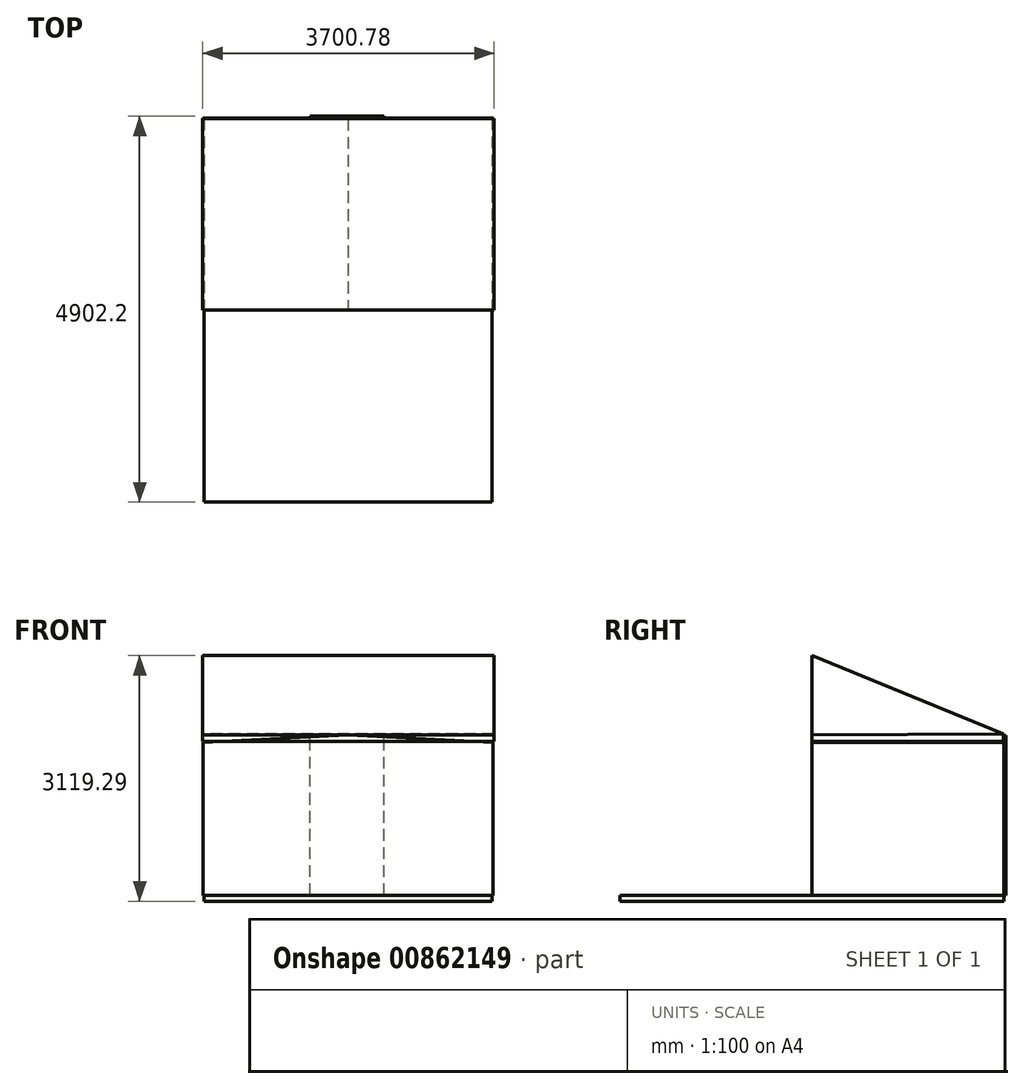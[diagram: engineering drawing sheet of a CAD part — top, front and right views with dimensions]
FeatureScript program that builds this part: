
annotation { "Feature Type Name" : "Feature", "Feature Type Description" : "" }
export const myFeature = defineFeature(function(context is Context, id is Id, definition is map)
    precondition{}
    {
        {
            var Q0;
            Q0=qCreatedBy(makeId("Top.planeOp"),FACE);
            var sketch = newSketch(context, id + "F0", { "sketchPlane" : qUnion([Q0])});
            skLineSegment(sketch, "E0.bottom", {"start": v(1828.8, 2438.4) * mm, "end": v(-1828.8, 2438.4) * mm});
            skLineSegment(sketch, "E0.top", {"start": v(1828.8, -2438.4) * mm, "end": v(-1828.8, -2438.4) * mm});
            skLineSegment(sketch, "E0.left", {"start": v(1828.8, 2438.4) * mm, "end": v(1828.8, -2438.4) * mm});
            skLineSegment(sketch, "E0.right", {"start": v(-1828.8, 2438.4) * mm, "end": v(-1828.8, -2438.4) * mm});
            skPoint(sketch, "E0.middle", {"position": v(0, 0) * mm});
            skPoint(sketch, "E1", {"position": v(1828.8, -2438.4) * mm});
            skPoint(sketch, "E2", {"position": v(-1828.8, -2438.4) * mm});
            skPoint(sketch, "E3", {"position": v(-1828.8, 2438.4) * mm});
            skPoint(sketch, "E4", {"position": v(1828.8, 2438.4) * mm});
            skSolve(sketch);
        }
        {
            var Q0;
            Q0=qCreatedBy(makeId("Front.planeOp"),FACE);
            var sketch = newSketch(context, id + "F1", { "sketchPlane" : qUnion([Q0])});
            skLineSegment(sketch, "E5", {"start": v(1843.43, 0) * mm, "end": v(1843.43, 1941.23) * mm});
            skLineSegment(sketch, "E6", {"start": v(1843.43, 1941.23) * mm, "end": v(0, 2036.83) * mm});
            skLineSegment(sketch, "E7", {"start": v(0, 2036.83) * mm, "end": v(-1839.49, 1941.23) * mm});
            skLineSegment(sketch, "E8", {"start": v(-1839.49, 1941.23) * mm, "end": v(-1839.49, 0) * mm});
            skLineSegment(sketch, "E9", {"start": v(1843.43, 0) * mm, "end": v(-1839.49, 0) * mm});
            skSolve(sketch);
        }
        {
            var Q0;
            Q0=makeQuery(id+"F1.imprint","IMPRINT",FACE,{"disambiguationData":[TD([[makeQuery(id+"F1.imprint","IMPRINT",EDGE,{"derivedFrom":sQuery(id+"F1.wireOp",EDGE,"E5")}),1.0]])]});
            extrude(context, id + "F2", {"entities" : qUnion([Q0]), "oppositeDirection" : true, "depth" : 2438.4 * mm, "offsetDistance" : 25.4 * mm});
        }
        {
            var Q0;
            Q0=qCreatedBy(makeId("Right.planeOp"),FACE);
            var sketch = newSketch(context, id + "F3", { "sketchPlane" : qUnion([Q0])});
            skLineSegment(sketch, "E10", {"start": v(2432.25, 2051.92) * mm, "end": v(0, 3043.09) * mm});
            skLineSegment(sketch, "E11", {"start": v(0, 3043.09) * mm, "end": v(0, 2036.83) * mm});
            skLineSegment(sketch, "E12", {"start": v(0, 2036.83) * mm, "end": v(2432.25, 2051.92) * mm});
            skSolve(sketch);
        }
        {
            var Q0;
            Q0=makeQuery(id+"F3.imprint","IMPRINT",FACE,{"disambiguationData":[TD([[makeQuery(id+"F3.imprint","IMPRINT",EDGE,{"derivedFrom":sQuery(id+"F3.wireOp",EDGE,"E10")}),1.0]])]});
            extrude(context, id + "F4", {"entities" : qUnion([Q0]), "depth" : 1856.74 * mm, "offsetDistance" : 25.4 * mm});
        }
        {
            var Q0;
            Q0=makeQuery(id+"F4.opExtrude","CAP_FACE",FACE,{"disambiguationData":[OSD([sQuery(id+"F3.wireOp",EDGE,"E10"),sQuery(id+"F3.wireOp",EDGE,"E11"),sQuery(id+"F3.wireOp",EDGE,"E12")])],"isStart":true});
            extrude(context, id + "F5", {"entities" : qUnion([Q0]), "operationType" : NewBodyOperationType.ADD, "depth" : 1844.04 * mm, "offsetDistance" : 25.4 * mm});
        }
        {
            var Q0;
            Q0=makeQuery(id+"F5.opExtrude","CAP_FACE",FACE,{"disambiguationData":[OSD([sQuery(id+"F3.wireOp",EDGE,"E10"),sQuery(id+"F3.wireOp",EDGE,"E11"),sQuery(id+"F3.wireOp",EDGE,"E12")])],"isStart":false});
            var sketch = newSketch(context, id + "F6", { "sketchPlane" : qUnion([Q0])});
            skLineSegment(sketch, "E13", {"start": v(-2432.25, 2051.92) * mm, "end": v(-2432.25, 1956.17) * mm});
            skLineSegment(sketch, "E14", {"start": v(-2432.25, 1956.17) * mm, "end": v(0, 1956.17) * mm});
            skLineSegment(sketch, "E15", {"start": v(0, 1956.17) * mm, "end": v(0, 2036.83) * mm});
            skLineSegment(sketch, "E16", {"start": v(0, 2036.83) * mm, "end": v(-2432.25, 2051.92) * mm});
            skSolve(sketch);
        }
        {
            var Q0;
            Q0=makeQuery(id+"F2.opExtrude","CAP_FACE",FACE,{"disambiguationData":[OSD([sQuery(id+"F1.wireOp",EDGE,"E5"),sQuery(id+"F1.wireOp",EDGE,"E6"),sQuery(id+"F1.wireOp",EDGE,"E7"),sQuery(id+"F1.wireOp",EDGE,"E8"),sQuery(id+"F1.wireOp",EDGE,"E9")])],"isStart":false});
            var sketch = newSketch(context, id + "F7", { "sketchPlane" : qUnion([Q0])});
            skLineSegment(sketch, "E17", {"start": v(-1843.43, 1941.23) * mm, "end": v(1839.49, 1941.23) * mm});
            skLineSegment(sketch, "E18", {"start": v(1839.49, 1941.23) * mm, "end": v(1839.49, 2036.83) * mm});
            skLineSegment(sketch, "E19", {"start": v(1839.49, 2036.83) * mm, "end": v(-1843.43, 2036.83) * mm});
            skLineSegment(sketch, "E20", {"start": v(-1843.43, 2036.83) * mm, "end": v(-1843.43, 1941.23) * mm});
            skSolve(sketch);
        }
        {
            var Q0;
            Q0=makeQuery(id+"F6.imprint","IMPRINT",FACE,{"disambiguationData":[TD([[makeQuery(id+"F6.imprint","IMPRINT",EDGE,{"derivedFrom":sQuery(id+"F6.wireOp",EDGE,"E13")}),1.0]])]});
            extrude(context, id + "F8", {"entities" : qUnion([Q0]), "oppositeDirection" : true, "depth" : 3700.78 * mm, "offsetDistance" : 25.4 * mm});
        }
        {
            var Q0;
            Q0=makeQuery(id+"F7.imprint","IMPRINT",FACE,{"disambiguationData":[TD([[makeQuery(id+"F7.imprint","IMPRINT",EDGE,{"derivedFrom":sQuery(id+"F7.wireOp",EDGE,"E17")}),-1.0]])]});
            var sketch = newSketch(context, id + "F9", { "sketchPlane" : qUnion([Q0])});
            skLineSegment(sketch, "E21", {"start": v(0, 0) * mm, "end": v(-457.2, 0) * mm});
            skLineSegment(sketch, "E22.bottom", {"start": v(-457.2, 0) * mm, "end": v(479.3, 0) * mm});
            skLineSegment(sketch, "E22.top", {"start": v(-457.2, 2032) * mm, "end": v(479.3, 2032) * mm});
            skLineSegment(sketch, "E22.left", {"start": v(-457.2, 0) * mm, "end": v(-457.2, 2032) * mm});
            skLineSegment(sketch, "E22.right", {"start": v(479.3, 0) * mm, "end": v(479.3, 2032) * mm});
            skSolve(sketch);
        }
        {
            var Q0;
            {var subQ0=sQuery(id+"F9.wireOp",EDGE,"E22.top");Q0=makeQuery(id+"F9.imprint","IMPRINT",FACE,{"disambiguationData":[TD([[makeQuery(id+"F9.imprint","IMPRINT",EDGE,{"derivedFrom":subQ0}),-1.0]])]});}
            var Q1;
            {var subQ0=sQuery(id+"F9.wireOp",EDGE,"E22.left");var subQ6=makeQuery(id+"F7.imprint","IMPRINT",EDGE,{"derivedFrom":sQuery(id+"F7.wireOp",EDGE,"E17")});var subQ7=makeQuery(id+"F9.imprint","INTERSECT",VERTEX,{"derivedFrom":[subQ6,subQ0]});Q1=makeQuery(id+"F9.imprint","IMPRINT",FACE,{"disambiguationData":[TD([[makeQuery(id+"F9.imprint","IMPRINT",EDGE,{"disambiguationData":[TD([[subQ7,-1.0]])],"derivedFrom":subQ6}),-1.0]])]});}
            extrude(context, id + "F10", {"entities" : qUnion([Q0, Q1]), "operationType" : NewBodyOperationType.ADD, "depth" : 25.4 * mm, "offsetDistance" : 25.4 * mm});
        }
        {
            var Q0;
            Q0=makeQuery(id+"F0.imprint","IMPRINT",FACE,{"disambiguationData":[TD([[makeQuery(id+"F0.imprint","IMPRINT",EDGE,{"derivedFrom":sQuery(id+"F0.wireOp",EDGE,"E0.bottom")}),1.0]])]});
            extrude(context, id + "F11", {"entities" : qUnion([Q0]), "operationType" : NewBodyOperationType.ADD, "oppositeDirection" : true, "depth" : 76.2 * mm, "offsetDistance" : 25.4 * mm});
        }
    });
